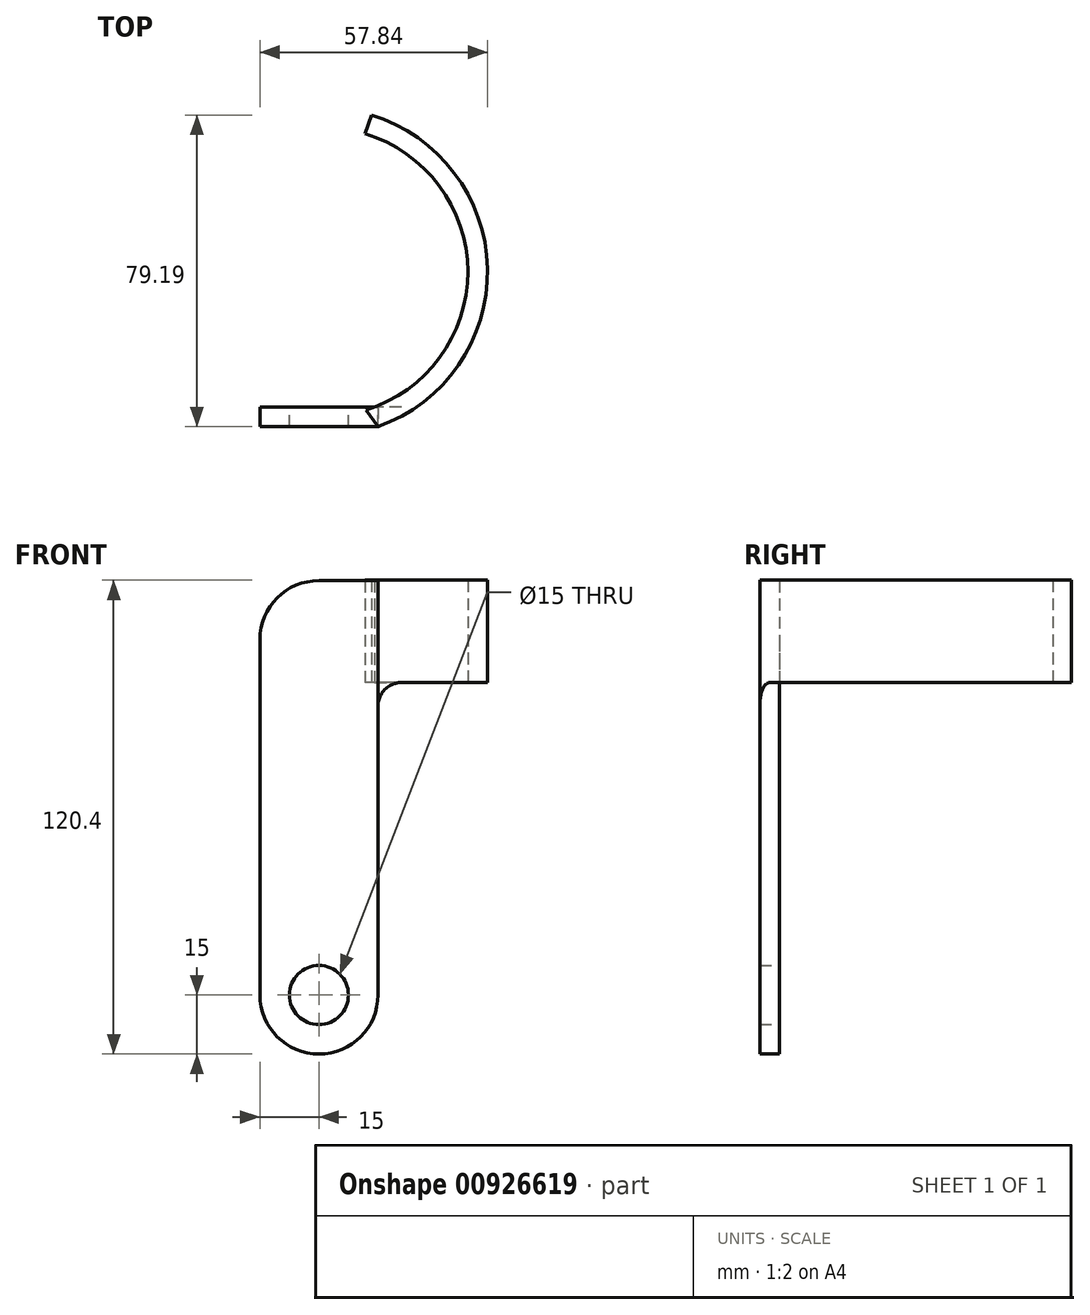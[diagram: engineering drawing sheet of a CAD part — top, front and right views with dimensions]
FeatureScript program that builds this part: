
annotation { "Feature Type Name" : "Feature", "Feature Type Description" : "" }
export const myFeature = defineFeature(function(context is Context, id is Id, definition is map)
    precondition{}
    {
        {
            var Q0;
            Q0=qCreatedBy(makeId("Front.planeOp"),FACE);
            var sketch = newSketch(context, id + "F0", { "sketchPlane" : qUnion([Q0])});
            skLineSegment(sketch, "E0.bottom", {"start": v(15, 25.9) * mm, "end": v(-15, 25.9) * mm});
            skLineSegment(sketch, "E0.top", {"start": v(15, -79.4) * mm, "end": v(-15, -79.4) * mm});
            skLineSegment(sketch, "E0.left", {"start": v(15, 25.9) * mm, "end": v(15, -79.4) * mm});
            skLineSegment(sketch, "E0.right", {"start": v(-15, 25.9) * mm, "end": v(-15, -79.4) * mm});
            skCircle(sketch, "E1", {"center": v(0, -79.4) * mm, "radius": 15 * mm});
            skCircle(sketch, "E2", {"center": v(0, -79.4) * mm, "radius": 7.5 * mm});
            skSolve(sketch);
        }
        {
            var Q0;
            Q0 = qSketchRegion(id + "F0", true);
            extrude(context, id + "F1", {"entities" : qUnion([Q0]), "depth" : 5 * mm, "offsetDistance" : 25 * mm});
        }
        {
            var Q0;
            Q0=qCreatedBy(makeId("Top.planeOp"),FACE);
            var sketch = newSketch(context, id + "F2", { "sketchPlane" : qUnion([Q0])});
            skArc(sketch, "E3", {"start": v(11.93, -0.75) * mm, "mid": v(37.84, 34.44) * mm, "end": v(11.7, 69.46) * mm});
            skArc(sketch, "E4.0", {"start": v(15, -5) * mm, "mid": v(42.83, 35.2) * mm, "end": v(13.31, 74.2) * mm});
            skLineSegment(sketch, "E5", {"start": v(13.31, 74.2) * mm, "end": v(11.7, 69.46) * mm});
            skLineSegment(sketch, "E6", {"start": v(15, -5) * mm, "end": v(11.93, -0.75) * mm});
            skPoint(sketch, "E7", {"position": v(15, -5) * mm});
            skSolve(sketch);
        }
        {
            var Q0;
            Q0=makeQuery(id+"F2.imprint","IMPRINT",FACE,{"disambiguationData":[TD([[makeQuery(id+"F2.imprint","IMPRINT",EDGE,{"derivedFrom":sQuery(id+"F2.wireOp",EDGE,"E3")}),-1.0]])]});
            extrude(context, id + "F3", {"entities" : qUnion([Q0]), "operationType" : NewBodyOperationType.ADD, "depth" : 26 * mm, "offsetDistance" : 25 * mm});
        }
        {
            var Q0;
            Q0=makeQuery(id+"F1.opExtrude","SWEPT_EDGE",EDGE,{"disambiguationData":[OSD([sQuery(id+"F0.wireOp",EDGE,"E0.bottom"),sQuery(id+"F0.wireOp",EDGE,"E0.right")])]});
            fillet(context, id + "F4", {"entities" : qUnion([Q0]), "radius" : 15 * mm, "tangentPropagation" : true, "allowEdgeOverflow" : false});
        }
        {
            var Q0;
            Q0=makeQuery(id+"F3.boolean.opBoolean","INTERSECT",EDGE,{"derivedFrom":[makeQuery(id+"F1.opExtrude","SWEPT_FACE",FACE,{"disambiguationData":[OSD([sQuery(id+"F0.wireOp",EDGE,"E0.left")])]}),makeQuery(id+"F3.opExtrude","CAP_FACE",FACE,{"disambiguationData":[OSD([sQuery(id+"F2.wireOp",EDGE,"E3"),sQuery(id+"F2.wireOp",EDGE,"E4.0"),sQuery(id+"F2.wireOp",EDGE,"E5"),sQuery(id+"F2.wireOp",EDGE,"E6")])],"isStart":true})]});
            fillet(context, id + "F5", {"entities" : qUnion([Q0]), "radius" : 6 * mm, "tangentPropagation" : true, "allowEdgeOverflow" : false});
        }
    });
